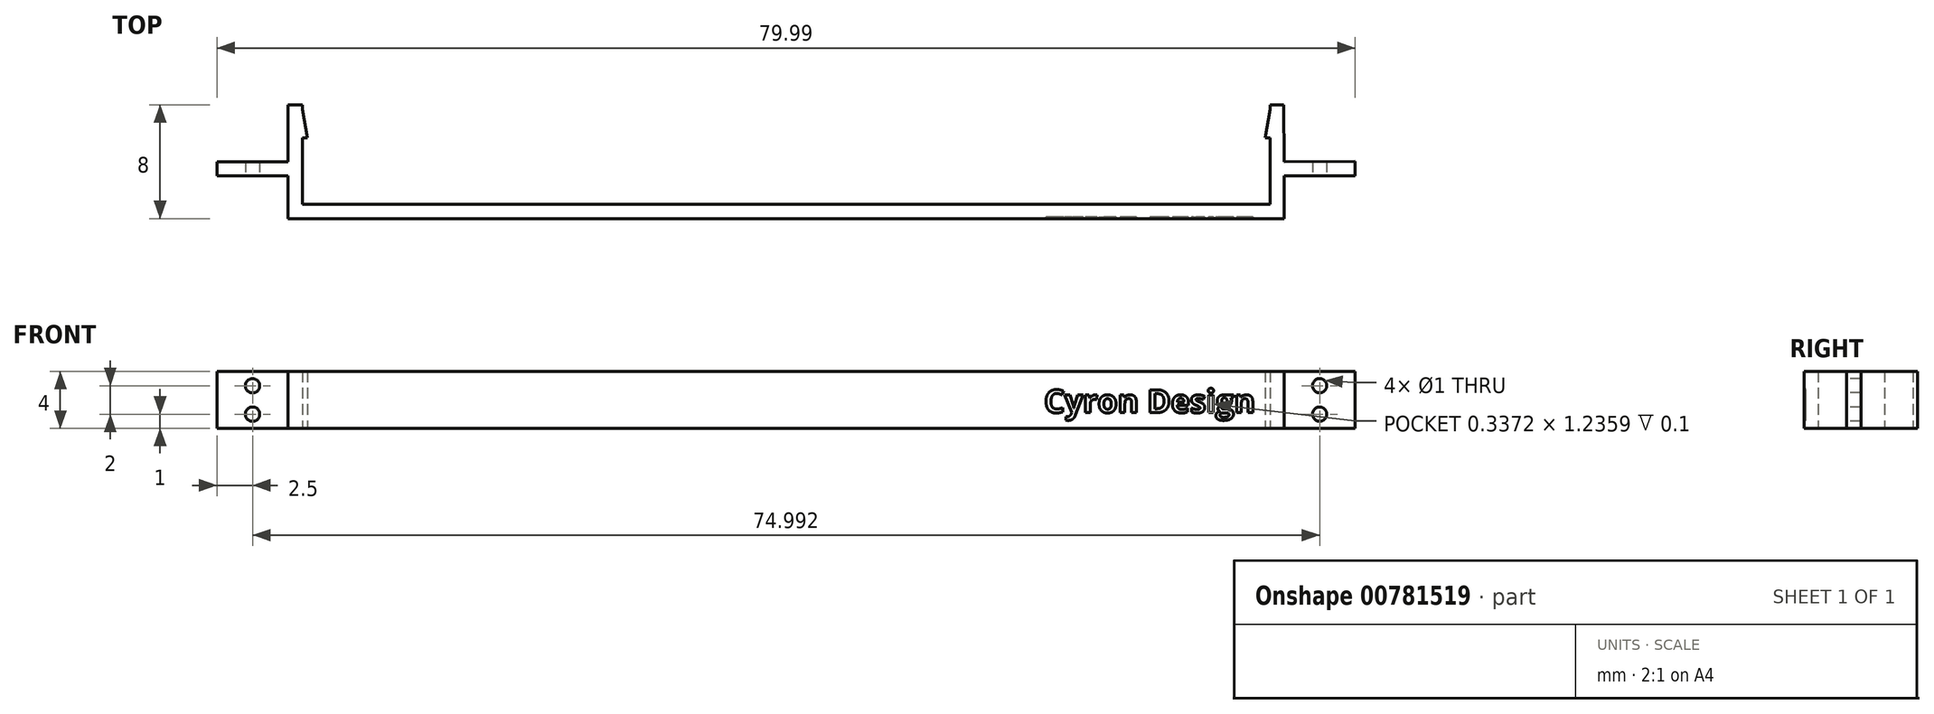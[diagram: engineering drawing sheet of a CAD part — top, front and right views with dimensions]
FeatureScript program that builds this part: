
annotation { "Feature Type Name" : "Feature", "Feature Type Description" : "" }
export const myFeature = defineFeature(function(context is Context, id is Id, definition is map)
    precondition{}
    {
        {
            var Q0;
            Q0=qCreatedBy(makeId("Top.planeOp"),FACE);
            var sketch = newSketch(context, id + "F0", { "sketchPlane" : qUnion([Q0])});
            skLineSegment(sketch, "E0.bottom", {"start": v(-34, -12.01) * mm, "end": v(-35, -12.01) * mm});
            skLineSegment(sketch, "E0.top", {"start": v(-34, -19.01) * mm, "end": v(-35, -19.01) * mm});
            skLineSegment(sketch, "E0.left", {"start": v(-34, -12.01) * mm, "end": v(-34, -19.01) * mm});
            skLineSegment(sketch, "E0.right", {"start": v(-35, -12.01) * mm, "end": v(-35, -19.01) * mm});
            skLineSegment(sketch, "E1.bottom", {"start": v(-35, -17.01) * mm, "end": v(-40, -17.01) * mm});
            skLineSegment(sketch, "E1.top", {"start": v(-35, -16.01) * mm, "end": v(-40, -16.01) * mm});
            skLineSegment(sketch, "E1.left", {"start": v(-35, -17.01) * mm, "end": v(-35, -16.01) * mm});
            skLineSegment(sketch, "E1.right", {"start": v(-40, -17.01) * mm, "end": v(-40, -16.01) * mm});
            skLineSegment(sketch, "E2.MirrorCS", {"start": v(35, -17.01) * mm, "end": v(34.99, -16.01) * mm});
            skLineSegment(sketch, "E3.MirrorCS", {"start": v(34, -12.01) * mm, "end": v(34.97, -12.01) * mm});
            skLineSegment(sketch, "E4.MirrorCS", {"start": v(40, -17) * mm, "end": v(39.99, -16) * mm});
            skLineSegment(sketch, "E5.MirrorCS", {"start": v(34, -19.01) * mm, "end": v(35, -19.01) * mm});
            skLineSegment(sketch, "E6.MirrorCS", {"start": v(35, -17.01) * mm, "end": v(40, -17) * mm});
            skLineSegment(sketch, "E7.MirrorCS", {"start": v(34.99, -16.01) * mm, "end": v(39.99, -16) * mm});
            skLineSegment(sketch, "E8.MirrorCS", {"start": v(34, -12.01) * mm, "end": v(34, -19.01) * mm});
            skLineSegment(sketch, "E9.MirrorCS", {"start": v(34.97, -12.01) * mm, "end": v(35, -19.01) * mm});
            skLineSegment(sketch, "E10.bottom", {"start": v(-35, -19.01) * mm, "end": v(35, -19.01) * mm});
            skLineSegment(sketch, "E10.top", {"start": v(-35, -20.01) * mm, "end": v(35, -20.01) * mm});
            skLineSegment(sketch, "E10.left", {"start": v(-35, -19.01) * mm, "end": v(-35, -20.01) * mm});
            skLineSegment(sketch, "E10.right", {"start": v(35, -19.01) * mm, "end": v(35, -20.01) * mm});
            skLineSegment(sketch, "E11", {"start": v(-34, -12.34) * mm, "end": v(-33.65, -14.34) * mm});
            skLineSegment(sketch, "E12", {"start": v(-33.65, -14.34) * mm, "end": v(-34, -14.34) * mm});
            skLineSegment(sketch, "E13", {"start": v(-34, -14.34) * mm, "end": v(-34, -12.34) * mm});
            skLineSegment(sketch, "E14", {"start": v(-34, -14.34) * mm, "end": v(-33.65, -14.34) * mm});
            skLineSegment(sketch, "E15.MirrorCS", {"start": v(34, -12.34) * mm, "end": v(33.65, -14.34) * mm});
            skLineSegment(sketch, "E16.MirrorCS", {"start": v(34, -14.34) * mm, "end": v(33.65, -14.34) * mm});
            skLineSegment(sketch, "E17.MirrorCS", {"start": v(34, -14.34) * mm, "end": v(34, -12.34) * mm});
            skLineSegment(sketch, "E18.MirrorCS", {"start": v(-34.01, -12.33) * mm, "end": v(-33.66, -14.33) * mm});
            skSolve(sketch);
        }
        {
            var Q0;
            Q0=makeQuery(id+"F0.imprint","IMPRINT",FACE,{"disambiguationData":[TD([[makeQuery(id+"F0.imprint","IMPRINT",EDGE,{"derivedFrom":sQuery(id+"F0.wireOp",EDGE,"E1.bottom")}),-1.0]])]});
            var Q1;
            {var subQ4=sQuery(id+"F0.wireOp",EDGE,"E0.bottom");Q1=makeQuery(id+"F0.imprint","IMPRINT",FACE,{"disambiguationData":[TD([[makeQuery(id+"F0.imprint","IMPRINT",EDGE,{"derivedFrom":subQ4}),1.0]])]});}
            var Q2;
            Q2=makeQuery(id+"F0.imprint","IMPRINT",FACE,{"disambiguationData":[TD([[makeQuery(id+"F0.imprint","IMPRINT",EDGE,{"derivedFrom":sQuery(id+"F0.wireOp",EDGE,"E10.top")}),1.0]])]});
            var Q3;
            Q3=makeQuery(id+"F0.imprint","IMPRINT",FACE,{"disambiguationData":[TD([[makeQuery(id+"F0.imprint","IMPRINT",EDGE,{"derivedFrom":sQuery(id+"F0.wireOp",EDGE,"E4.MirrorCS")}),1.0]])]});
            var Q4;
            {var subQ4=sQuery(id+"F0.wireOp",EDGE,"E3.MirrorCS");Q4=makeQuery(id+"F0.imprint","IMPRINT",FACE,{"disambiguationData":[TD([[makeQuery(id+"F0.imprint","IMPRINT",EDGE,{"derivedFrom":subQ4}),-1.0]])]});}
            var Q5;
            Q5=makeQuery(id+"F0.imprint","IMPRINT",FACE,{"disambiguationData":[TD([[makeQuery(id+"F0.imprint","IMPRINT",EDGE,{"derivedFrom":sQuery(id+"F0.wireOp",EDGE,"E15.MirrorCS")}),1.0]])]});
            var Q6;
            {var subQ0=sQuery(id+"F0.wireOp",EDGE,"E14");var subQ3=sQuery(id+"F0.wireOp",EDGE,"E18.MirrorCS");var subQ5=makeQuery(id+"F0.imprint","INTERSECT",VERTEX,{"derivedFrom":[subQ0,subQ3]});Q6=makeQuery(id+"F0.imprint","IMPRINT",FACE,{"disambiguationData":[TD([[makeQuery(id+"F0.imprint","IMPRINT",EDGE,{"disambiguationData":[TD([[subQ5,1.0]])],"derivedFrom":subQ3}),-1.0]])]});}
            var Q7;
            {var subQ0=sQuery(id+"F0.wireOp",EDGE,"E11");Q7=makeQuery(id+"F0.imprint","IMPRINT",FACE,{"disambiguationData":[TD([[makeQuery(id+"F0.imprint","IMPRINT",EDGE,{"derivedFrom":subQ0}),-1.0]])]});}
            extrude(context, id + "F1", {"entities" : qUnion([Q0, Q1, Q2, Q3, Q4, Q5, Q6, Q7]), "depth" : 5 * mm, "offsetDistance" : 25 * mm, "hasSecondDirection" : true, "secondDirectionOppositeDirection" : false, "secondDirectionDepth" : 1 * mm});
        }
        {
            var Q0;
            Q0=makeQuery(id+"F1.opExtrude","SWEPT_FACE",FACE,{"disambiguationData":[OSD([sQuery(id+"F0.wireOp",EDGE,"E1.bottom")])]});
            var sketch = newSketch(context, id + "F2", { "sketchPlane" : qUnion([Q0])});
            skCircle(sketch, "E19", {"center": v(-37.5, 4) * mm, "radius": 0.5 * mm});
            skCircle(sketch, "E20", {"center": v(-37.5, 2) * mm, "radius": 0.5 * mm});
            skSolve(sketch);
        }
        {
            var Q0;
            Q0=sQuery(id+"F2.wireOp",VERTEX,"E19.center");
            var Q1;
            Q1=sQuery(id+"F2.wireOp",VERTEX,"E20.center");
            var Q2;
            Q2=makeQuery(id+"F1.opExtrude","SWEPT_BODY",BODY,{"disambiguationData":[OSD([sQuery(id+"F0.wireOp",EDGE,"E0.bottom"),sQuery(id+"F0.wireOp",EDGE,"E0.left"),sQuery(id+"F0.wireOp",EDGE,"E0.right"),sQuery(id+"F0.wireOp",EDGE,"E1.bottom"),sQuery(id+"F0.wireOp",EDGE,"E1.top"),sQuery(id+"F0.wireOp",EDGE,"E1.right"),sQuery(id+"F0.wireOp",EDGE,"E3.MirrorCS"),sQuery(id+"F0.wireOp",EDGE,"E4.MirrorCS"),sQuery(id+"F0.wireOp",EDGE,"E6.MirrorCS"),sQuery(id+"F0.wireOp",EDGE,"E7.MirrorCS"),sQuery(id+"F0.wireOp",EDGE,"E8.MirrorCS"),sQuery(id+"F0.wireOp",EDGE,"E9.MirrorCS"),sQuery(id+"F0.wireOp",EDGE,"E10.bottom"),sQuery(id+"F0.wireOp",EDGE,"E10.top"),sQuery(id+"F0.wireOp",EDGE,"E10.left"),sQuery(id+"F0.wireOp",EDGE,"E10.right")])]});
            hole(context, id + "F3", {"style" : HoleStyle.SIMPLE, "endStyle" : HoleEndStyle.THROUGH, "holeDiameter" : 1 * mm, "majorDiameter" : 5 * mm, "isTappedThrough" : true, "tappedDepth" : 12 * mm, "tapClearance" : 3, "locations" : qUnion([Q0, Q1]), "scope" : qUnion([Q2])});
        }
        {
            var Q0;
            Q0=makeQuery(id+"F1.opExtrude","SWEPT_FACE",FACE,{"disambiguationData":[OSD([sQuery(id+"F0.wireOp",EDGE,"E6.MirrorCS")])]});
            var sketch = newSketch(context, id + "F4", { "sketchPlane" : qUnion([Q0])});
            skPoint(sketch, "E21", {"position": v(37.48, 4) * mm});
            skPoint(sketch, "E22", {"position": v(37.48, 2) * mm});
            skSolve(sketch);
        }
        {
            var Q0;
            Q0=sQuery(id+"F4.wireOp",VERTEX,"E22");
            var Q1;
            Q1=sQuery(id+"F4.wireOp",VERTEX,"E21");
            var Q2;
            Q2=makeQuery(id+"F1.opExtrude","SWEPT_BODY",BODY,{"disambiguationData":[OSD([sQuery(id+"F0.wireOp",EDGE,"E0.bottom"),sQuery(id+"F0.wireOp",EDGE,"E0.left"),sQuery(id+"F0.wireOp",EDGE,"E0.right"),sQuery(id+"F0.wireOp",EDGE,"E1.bottom"),sQuery(id+"F0.wireOp",EDGE,"E1.top"),sQuery(id+"F0.wireOp",EDGE,"E1.right"),sQuery(id+"F0.wireOp",EDGE,"E3.MirrorCS"),sQuery(id+"F0.wireOp",EDGE,"E4.MirrorCS"),sQuery(id+"F0.wireOp",EDGE,"E6.MirrorCS"),sQuery(id+"F0.wireOp",EDGE,"E7.MirrorCS"),sQuery(id+"F0.wireOp",EDGE,"E8.MirrorCS"),sQuery(id+"F0.wireOp",EDGE,"E9.MirrorCS"),sQuery(id+"F0.wireOp",EDGE,"E10.bottom"),sQuery(id+"F0.wireOp",EDGE,"E10.top"),sQuery(id+"F0.wireOp",EDGE,"E10.left"),sQuery(id+"F0.wireOp",EDGE,"E10.right")])]});
            hole(context, id + "F5", {"style" : HoleStyle.SIMPLE, "endStyle" : HoleEndStyle.THROUGH, "holeDiameter" : 1 * mm, "majorDiameter" : 5 * mm, "isTappedThrough" : true, "tappedDepth" : 12 * mm, "tapClearance" : 3, "locations" : qUnion([Q0, Q1]), "scope" : qUnion([Q2])});
        }
        {
            var Q0;
            Q0=makeQuery(id+"F1.opExtrude","SWEPT_FACE",FACE,{"disambiguationData":[OSD([sQuery(id+"F0.wireOp",EDGE,"E10.top")])]});
            var sketch = newSketch(context, id + "F6", { "sketchPlane" : qUnion([Q0])});
            skText(sketch, "E23", { "text": "Cyron Design", "fontName": "OpenSans-Bold.ttf"});
            const initialGuessF6  = {"E23": [0.01813, 0.0021, 1, 0, 0.00163]};
            skSetInitialGuess(sketch, initialGuessF6);
            skSolve(sketch);
        }
        {
            var Q0;
            Q0=qSketchRegion(id+"F6",true);
            extrude(context, id + "F7", {"entities" : qUnion([Q0]), "operationType" : NewBodyOperationType.REMOVE, "oppositeDirection" : true, "depth" : .1 * mm, "offsetDistance" : 25 * mm});
        }
    });
